# Revit family: Box Lean DI - Ceiling based
name_source: partatom
category: Lighting Fixtures
revit_build: Autodesk Revit Architecture 2014 (Build: 20130308_1515(x64)
units: mm (PartAtom-declared; Revit-internal decimal feet)

## types (2) — shared parameters
ArticleNumber = See URL hyperlink
AssetType = Moveable/Fixed
BSAB 96 = SNB.2
BallastsCELMAEnergyEfficiencyIndex = Class A1/A2
CCSClassCode = UAC
CCSClassName = Belysningsarmatur
CCSTopnode = L
Cassette Depth = 0 mm
Cassette Width = 0 mm
Color Filter = 16777215
Colour = White
ControlGearPosition = Integrated
Description = 70-80-35 General Lighting Systems
Dimming Lamp Color Temperature Shift = <None>
DocumentReference = See URL hyperlink
Documentation = See URL hyperlink
Finish = Powder coated
Frame = Riegens_Steel_Powder coated white RAL901025
Frame Depth = 142 mm
Glass = Riegens_Glass_opal
HasProtectiveEarth = TRUE
Height 1 = 81 mm
IfcExportAs = IfcLightFixtureType
IfcExportType = NOTDEFINED
InsulationStandardClass = Class 1
InternalFuse = Only required in emergency versions
LampColourRenderingIndex = Ra>80
LampType = LED
LightFixtureMountingType = Suspended
LightFixturePlacingType = Ceiling
LightSource = LED 3000K / 4000K
LuminairePowerFactor = >0,9
LuminaireType = Direct/Indirect LED Luminaire
Manufacturer = Riegens A/S
ManufacturerURL = www.riegens.com
Material = Steel, lens optic in PMMA, double parabolic louvre in Miro finish
NominalVoltage = 220-240V
Optic = Satin-matt double parabolic louvre (DP-SM)
PhaseReference = IEC recommendations
PhotometricPerformance = In accordance with BS EN 13032-1
ProductInformation = http://riegens.com
Shape = Rectangle
Tilt Angle = 90.00°
Uniclass 1.4 = JY73
Uniclass2 = Pr_70_70_49_43 Light-Emitting Diode (LED) Luminaires
Version = v.1.0
Void = Yes

## per-type parameters (varying)
| type | BIMObjectName | Fixing point Suspended | Frame Width | LampRating | Photometric Web File | Size | Suspended Distance | Suspended Distance Bottom | TotalWattage |
| Box Lean DI 1500 | Box Lean DI 1500.rfa | 1200 mm | 1500 mm | 44W | Box Lean 1500 DI 44W 4000K DP Satinmatt.ies | 142 x 1500 x 81 mm | 500 mm | 581 mm | Max. 46W |
| Box Lean DI 1200 | Box Lean DI 1200.rfa | 900 mm | 1200 mm | 28W / 38W | Box Lean 1200 DI 38W 4000K DP Satinmatt.ies | 142 x 1200 x 81 mm | 600 mm | 681 mm | Max. 30W / 40W |

note: column(s) folded — value = type name in every type: ModelReference

## geometry (parser evidence)
native form markers: Blend x90, Sweep x6
no freeform markers — native parametric forms only
